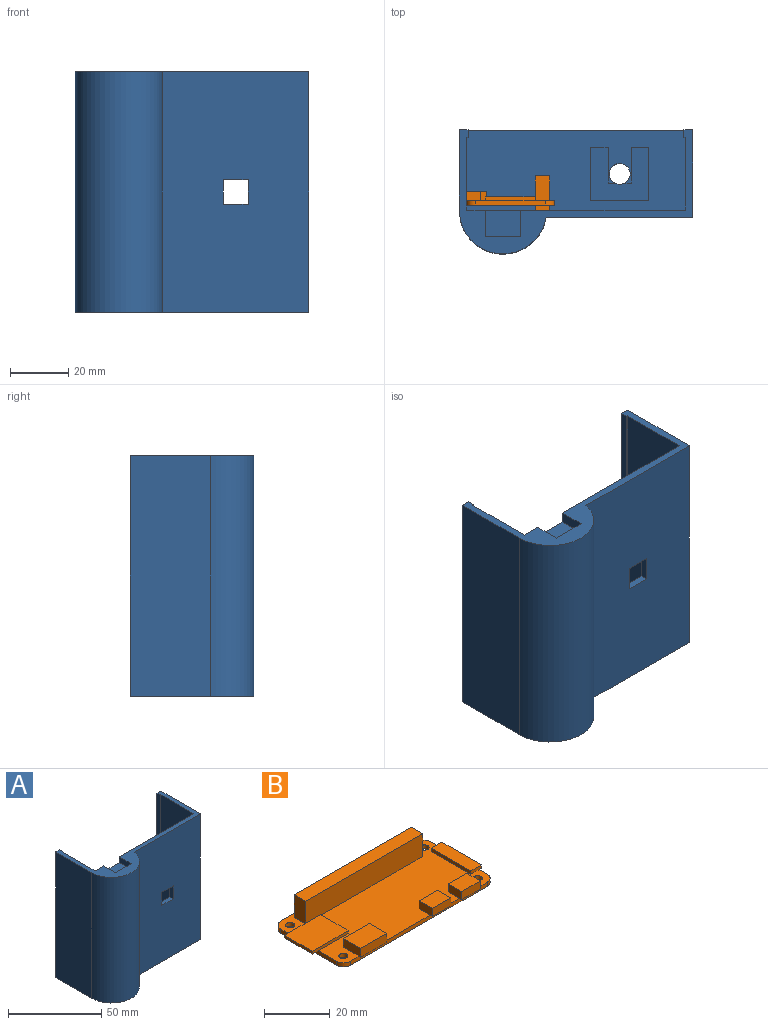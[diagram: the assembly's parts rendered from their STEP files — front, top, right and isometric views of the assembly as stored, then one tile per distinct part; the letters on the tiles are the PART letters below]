
ASSEMBLY  parts=2 mates=3
PART A: 40 faces, bbox 80x42.5x82.5 mm
  f0: cylinder r=3.56mm len=3.43mm, axis (0,0,1), area 7.3mm2, adj f32,f33,f34,f39
  f1: plane 75x27.5mm, normal (0,0,1), area 1816.5mm2, adj f3,f5,f9,f10,f11,f12,f13,f14
  f2: plane 82.5x50.21mm, normal (0,-1,0), area 4070.1mm2, adj f4,f7,f8,f15,f20,f21,f22,f23
  f3: plane 80x75mm, normal (0,1,0), area 5882.8mm2, adj f1,f13,f14,f15,f16,f17,f18,f20
  f4: plane 82.5x30mm, normal (1,0,0), area 2475mm2, adj f2,f5,f8,f15
  f5: plane 82.5x80mm, normal (0,1,0), area 680mm2, adj f1,f4,f6,f8,f10,f11,f15
  f6: plane 82.5x27.5mm, normal (-1,0,0), area 2268.8mm2, adj f5,f7,f8,f15
  f7: cylinder r=15mm len=82.5mm, axis (0,0,1), area 3680.5mm2, adj f2,f6,f8,f15
  f8: plane 80x42.5mm, normal (0,0,-1), area 2638.9mm2, adj f2,f4,f5,f6,f7,f24
  f9: plane 80x0.5mm, normal (0,-1,0), area 40mm2, adj f1,f10,f14,f15
  f10: plane 80x2.5mm, normal (1,0,0), area 200mm2, adj f1,f5,f9,f15
  f11: plane 80x2.5mm, normal (-1,0,0), area 200mm2, adj f1,f5,f12,f15
  f12: plane 80x0.5mm, normal (0,-1,0), area 40mm2, adj f1,f11,f13,f15
  f13: plane 80x25mm, normal (-1,0,0), area 2000mm2, adj f1,f3,f12,f15
  f14: plane 80x25mm, normal (1,0,0), area 2000mm2, adj f1,f3,f9,f15
  f15: plane 80x42.5mm, normal (0,0,1), area 510.6mm2, adj f2,f3,f4,f5,f6,f7,f9,f10
  f16: plane 12x9mm, normal (0,0,1), area 108mm2, adj f3,f17,f18,f19
  f17: plane 9x3.75mm, normal (1,0,0), area 33.8mm2, adj f3,f15,f16,f19
  f18: plane 9x3.75mm, normal (-1,0,0), area 33.8mm2, adj f3,f15,f16,f19
  f19: plane 12x3.75mm, normal (0,1,0), area 45mm2, adj f15,f16,f17,f18
  f20: plane 8.5x2.5mm, normal (0,0,1), area 21.3mm2, adj f2,f3,f21,f23
  f21: plane 8.5x2.5mm, normal (-1,0,0), area 21.2mm2, adj f2,f3,f20,f22
  f22: plane 8.5x2.5mm, normal (0,0,-1), area 21.3mm2, adj f2,f3,f21,f23
  f23: plane 8.5x2.5mm, normal (1,0,0), area 21.2mm2, adj f2,f3,f20,f22
  f24: cylinder r=3.56mm len=7.11mm, axis (0,0,1), area 55.9mm2, adj f1,f8
  f25: plane 12.23x2.03mm, normal (1,0,0), area 24.8mm2, adj f26,f33,f34,f39
  f26: plane 7.62x6mm, normal (0,1,0), area 36.1mm2, adj f1,f25,f27,f34,f35,f39
  f27: plane 18.23x7.62mm, normal (-1,0,0), area 138.9mm2, adj f1,f26,f28,f34
  f28: plane 20x7.62mm, normal (0,-1,0), area 152.4mm2, adj f1,f27,f29,f34
  f29: plane 18.23x7.62mm, normal (1,0,0), area 138.9mm2, adj f1,f28,f30,f34
  f30: plane 7.62x6mm, normal (0,1,0), area 36.1mm2, adj f1,f29,f31,f34,f38,f39
  f31: plane 12.23x2.03mm, normal (-1,0,0), area 24.8mm2, adj f30,f32,f34,f39
  f32: plane 2.28x2.03mm, normal (0,1,0), area 4.6mm2, adj f0,f31,f34,f39
  f33: plane 2.28x2.03mm, normal (0,1,0), area 4.6mm2, adj f0,f25,f34,f39
  f34: plane 20x18.23mm, normal (0,0,1), area 265.7mm2, adj f0,f25,f26,f27,f28,f29,f30,f31
  f35: plane 12.41x5.59mm, normal (1,0,0), area 69.4mm2, adj f1,f26,f36,f39
  f36: plane 5.72x5.59mm, normal (0.5,0.87,0), area 36.9mm2, adj f1,f35,f37,f39
  f37: plane 5.72x5.59mm, normal (-0.5,0.87,0), area 36.9mm2, adj f1,f36,f38,f39
  f38: plane 12.41x5.59mm, normal (-1,0,0), area 69.4mm2, adj f1,f30,f37,f39
  f39: plane 15.71x11.43mm, normal (0,0,-1), area 61.9mm2, adj f0,f25,f26,f30,f31,f32,f33,f35
PART B: 54 faces, bbox 68.5x31x11.8 mm
  f0: plane 65x30mm, normal (0,0,1), area 1298.6mm2, adj f2,f3,f4,f5,f6,f7,f8,f9
  f1: plane 65x30mm, normal (0,0,-1), area 1666mm2, adj f2,f3,f4,f5,f6,f7,f8,f9
  f2: plane 59x1.5mm, normal (0,-1,0), area 88.5mm2, adj f0,f1,f3,f12,f30,f36,f42
  f3: cylinder r=3mm len=3mm, axis (0,0,1), area 7.1mm2, adj f0,f1,f2,f4
  f4: plane 24x1.5mm, normal (1,0,0), area 36mm2, adj f0,f1,f3,f5,f48
  f5: cylinder r=3mm len=3mm, axis (0,0,1), area 7.1mm2, adj f0,f1,f4,f6
  f6: plane 59x1.5mm, normal (0,1,0), area 88.5mm2, adj f0,f1,f5,f7
  f7: cylinder r=3mm len=3mm, axis (0,0,1), area 7.1mm2, adj f0,f1,f6,f8
  f8: plane 24x1.5mm, normal (-1,0,0), area 36mm2, adj f0,f1,f7,f12,f19
  f9: cylinder r=1.38mm len=2.75mm, axis (0,0,1), area 13mm2, adj f0,f1
  f10: cylinder r=1.38mm len=2.75mm, axis (0,0,1), area 13mm2, adj f0,f1
  f11: cylinder r=1.38mm len=2.75mm, axis (0,0,1), area 13mm2, adj f0,f1
  f12: cylinder r=3mm len=3mm, axis (0,0,1), area 7.1mm2, adj f0,f1,f2,f8
  f13: cylinder r=1.38mm len=2.75mm, axis (0,0,1), area 13mm2, adj f0,f1
  f14: plane 50.5x1.75mm, normal (0,-1,0), area 88.4mm2, adj f1,f15,f17,f18
  f15: plane 5x1.75mm, normal (1,0,0), area 8.7mm2, adj f1,f14,f16,f18
  f16: plane 50.5x1.75mm, normal (0,1,0), area 88.4mm2, adj f1,f15,f17,f18
  f17: plane 5x1.75mm, normal (-1,0,0), area 8.7mm2, adj f1,f14,f16,f18
  f18: plane 50.5x5mm, normal (0,0,-1), area 252.5mm2, adj f14,f15,f16,f17
  f19: plane 12x2.5mm, normal (0,0,-1), area 30mm2, adj f8,f20,f21,f22
  f20: plane 15.5x1mm, normal (0,1,0), area 15.5mm2, adj f0,f19,f21,f23,f24
  f21: plane 12x1mm, normal (-1,0,0), area 12mm2, adj f19,f20,f22,f24
  f22: plane 15.5x1mm, normal (0,-1,0), area 15.5mm2, adj f0,f19,f21,f23,f24
  f23: plane 12x1mm, normal (1,0,0), area 12mm2, adj f0,f20,f22,f24
  f24: plane 15.5x12mm, normal (0,0,1), area 186mm2, adj f20,f21,f22,f23
  f25: plane 7.5x3.25mm, normal (1,0,0), area 24.4mm2, adj f0,f26,f28,f29,f30
  f26: plane 11.25x3.25mm, normal (0,1,0), area 36.6mm2, adj f0,f25,f27,f29
  f27: plane 7.5x3.25mm, normal (-1,0,0), area 24.4mm2, adj f0,f26,f28,f29,f30
  f28: plane 11.25x3.25mm, normal (0,-1,0), area 36.6mm2, adj f25,f27,f29,f30
  f29: plane 11.25x7.5mm, normal (0,0,1), area 84.4mm2, adj f25,f26,f27,f28
  f30: plane 11.25x0.75mm, normal (0,0,-1), area 8.4mm2, adj f2,f25,f27,f28
  f31: plane 5.75x3mm, normal (1,0,0), area 17.2mm2, adj f0,f32,f34,f35,f36
  f32: plane 8x3mm, normal (0,1,0), area 24mm2, adj f0,f31,f33,f35
  f33: plane 5.75x3mm, normal (-1,0,0), area 17.2mm2, adj f0,f32,f34,f35,f36
  f34: plane 8x3mm, normal (0,-1,0), area 24mm2, adj f31,f33,f35,f36
  f35: plane 8x5.75mm, normal (0,0,1), area 46mm2, adj f31,f32,f33,f34
  f36: plane 8x1mm, normal (0,0,-1), area 8mm2, adj f2,f31,f33,f34
  f37: plane 8x3mm, normal (0,-1,0), area 24mm2, adj f38,f40,f41,f42
  f38: plane 5.75x3mm, normal (1,0,0), area 17.2mm2, adj f0,f37,f39,f41,f42
  f39: plane 8x3mm, normal (0,1,0), area 24mm2, adj f0,f38,f40,f41
  f40: plane 5.75x3mm, normal (-1,0,0), area 17.2mm2, adj f0,f37,f39,f41,f42
  f41: plane 8x5.75mm, normal (0,0,1), area 46mm2, adj f37,f38,f39,f40
  f42: plane 8x1mm, normal (0,0,-1), area 8mm2, adj f2,f37,f38,f40
  f43: plane 4.5x1.25mm, normal (0,-1,0), area 5.6mm2, adj f0,f44,f46,f47,f48
  f44: plane 17x1.25mm, normal (1,0,0), area 21.2mm2, adj f43,f45,f47,f48
  f45: plane 4.5x1.25mm, normal (0,1,0), area 5.6mm2, adj f0,f44,f46,f47,f48
  f46: plane 17x1.25mm, normal (-1,0,0), area 21.2mm2, adj f0,f43,f45,f47
  f47: plane 17x4.5mm, normal (0,0,1), area 76.5mm2, adj f43,f44,f45,f46
  f48: plane 17x1mm, normal (0,0,-1), area 17mm2, adj f4,f43,f44,f45
  f49: plane 50.5x8.5mm, normal (0,-1,0), area 429.2mm2, adj f0,f50,f52,f53
  f50: plane 8.5x5mm, normal (1,0,0), area 42.5mm2, adj f0,f49,f51,f53
  f51: plane 50.5x8.5mm, normal (0,1,0), area 429.2mm2, adj f0,f50,f52,f53
  f52: plane 8.5x5mm, normal (-1,0,0), area 42.5mm2, adj f0,f49,f51,f53
  f53: plane 50.5x5mm, normal (0,0,1), area 252.5mm2, adj f49,f50,f51,f52
PLACE A t=(0,10,0)mm
PLACE B rot(axis=(-0.58,-0.58,-0.58),120deg) t=(-22.5,0.75,35)mm
MATE planar B.f2 <-> A.f14  axis (-1,0,0) through (-37.5,0,35)mm
MATE planar B.f18 <-> A.f3  axis (0,-1,0) through (-11.5,-2.5,35)mm
MATE planar B.f21 <-> A.f1  axis (0,0,-1) through (-20.6,1.25,0)mm
